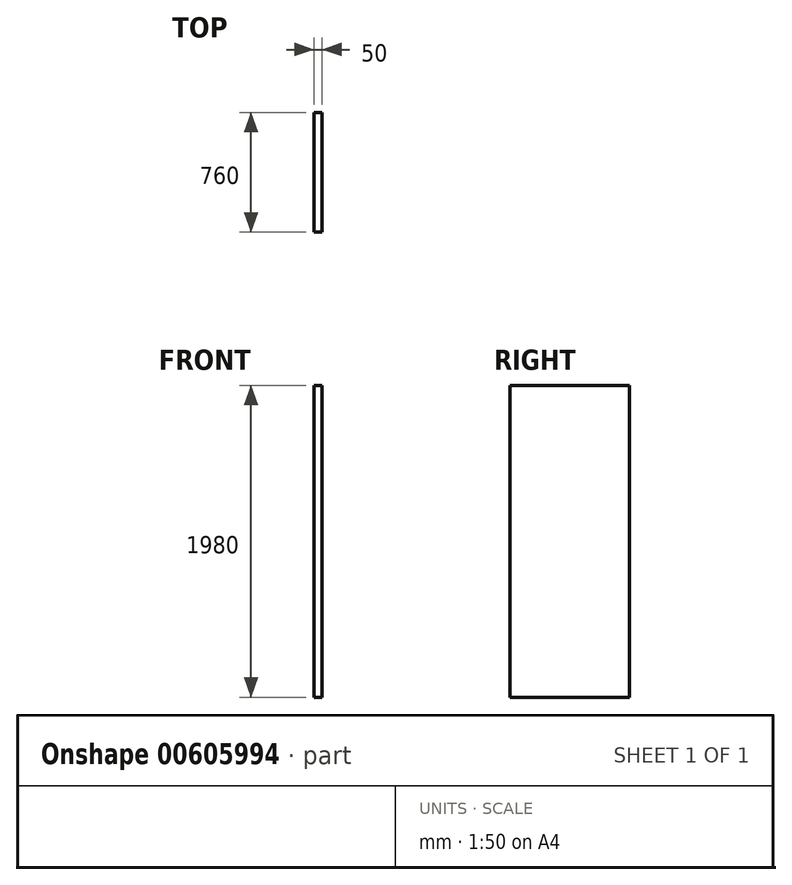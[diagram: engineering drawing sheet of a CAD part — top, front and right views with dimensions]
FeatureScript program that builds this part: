
annotation { "Feature Type Name" : "Feature", "Feature Type Description" : "" }
export const myFeature = defineFeature(function(context is Context, id is Id, definition is map)
    precondition{}
    {
        {
            var Q0;
            Q0=qCreatedBy(makeId("Right.planeOp"),FACE);
            var sketch = newSketch(context, id + "F0", { "sketchPlane" : qUnion([Q0])});
            skLineSegment(sketch, "E0.bottom", {"start": v(-423.37, 1121.08) * mm, "end": v(336.63, 1121.08) * mm});
            skLineSegment(sketch, "E0.top", {"start": v(-423.37, -858.92) * mm, "end": v(336.63, -858.92) * mm});
            skLineSegment(sketch, "E0.left", {"start": v(-423.37, 1121.08) * mm, "end": v(-423.37, -858.92) * mm});
            skLineSegment(sketch, "E0.right", {"start": v(336.63, 1121.08) * mm, "end": v(336.63, -858.92) * mm});
            skSolve(sketch);
        }
        {
            var Q0;
            Q0 = qSketchRegion(id + "F0", true);
            extrude(context, id + "F1", {"entities" : qUnion([Q0]), "depth" : 50 * mm, "offsetDistance" : 25 * mm});
        }
    });
